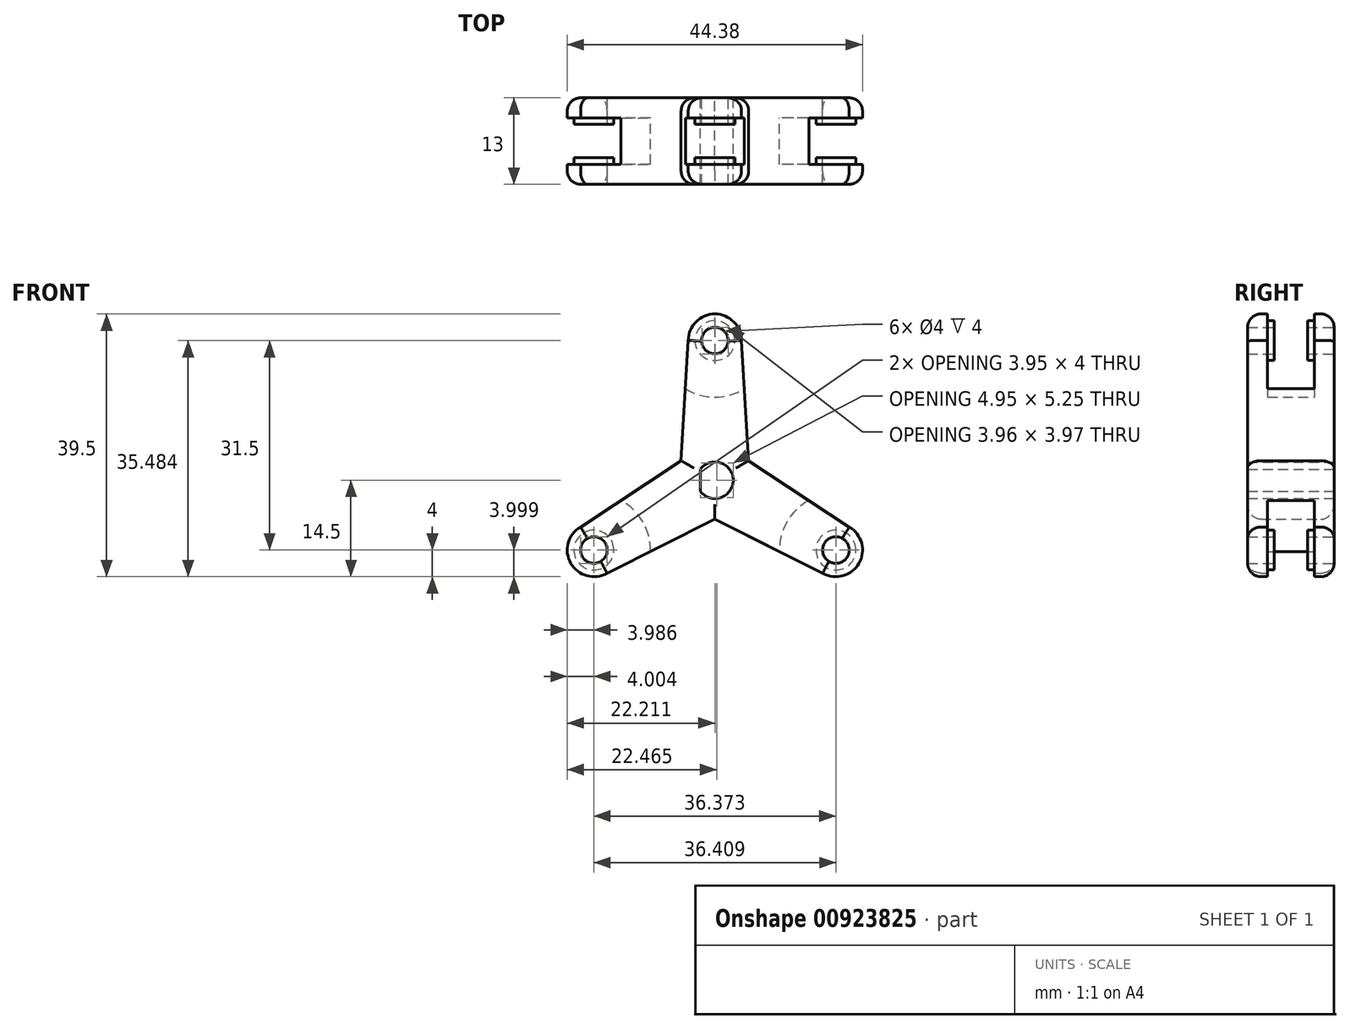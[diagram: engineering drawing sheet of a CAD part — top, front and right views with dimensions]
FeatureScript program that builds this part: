
annotation { "Feature Type Name" : "Feature", "Feature Type Description" : "" }
export const myFeature = defineFeature(function(context is Context, id is Id, definition is map)
    precondition{}
    {
        {
            var Q0;
            Q0=qCreatedBy(makeId("Front.planeOp"),FACE);
            var sketch = newSketch(context, id + "F0", { "sketchPlane" : qUnion([Q0])});
            skPoint(sketch, "E0", {"position": v(0, 27.5) * mm});
            skArc(sketch, "E1", {"start": v(-2.2, -1.65) * mm, "mid": v(2.75, 0) * mm, "end": v(-2.2, 1.65) * mm});
            skLineSegment(sketch, "E2", {"start": v(-2.2, 0) * mm, "end": v(-2.2, 1.65) * mm});
            skLineSegment(sketch, "E3", {"start": v(-2.2, 0) * mm, "end": v(-2.2, -1.65) * mm});
            skPoint(sketch, "E4", {"position": v(0, 21) * mm});
            skCircle(sketch, "E5", {"center": v(0, 21) * mm, "radius": 2 * mm});
            skCircle(sketch, "E6", {"center": v(0, 21) * mm, "radius": 3 * mm});
            skArc(sketch, "E7", {"start": v(-4.43, 13.75) * mm, "mid": v(0, 12.5) * mm, "end": v(4.43, 13.75) * mm});
            skPoint(sketch, "E8", {"position": v(0, 25) * mm});
            skArc(sketch, "E9", {"start": v(4, 21) * mm, "mid": v(0, 25) * mm, "end": v(-4, 21) * mm});
            skPoint(sketch, "E10", {"position": v(-4, 21) * mm});
            skPoint(sketch, "E11", {"position": v(4, 21) * mm});
            skLineSegment(sketch, "E12", {"start": v(-4, 21) * mm, "end": v(-5.26, 0) * mm});
            skLineSegment(sketch, "E13.MirrorCS", {"start": v(4, 21) * mm, "end": v(5.26, 0) * mm});
            skCircle(sketch, "E14.1.0", {"center": v(-18.19, -10.5) * mm, "radius": 2 * mm});
            skCircle(sketch, "E14.1.1", {"center": v(-18.19, -10.5) * mm, "radius": 3 * mm});
            skPoint(sketch, "E14.1.2", {"position": v(-20.19, -7.04) * mm});
            skPoint(sketch, "E14.1.3", {"position": v(-21.65, -12.5) * mm});
            skArc(sketch, "E14.1.4", {"start": v(-9.69, -10.71) * mm, "mid": v(-10.83, -6.25) * mm, "end": v(-14.12, -3.03) * mm});
            skArc(sketch, "E14.1.5", {"start": v(-20.19, -7.04) * mm, "mid": v(-21.65, -12.5) * mm, "end": v(-16.19, -13.96) * mm});
            skPoint(sketch, "E14.1.6", {"position": v(-16.19, -13.96) * mm});
            skLineSegment(sketch, "E14.1.7", {"start": v(-16.19, -13.96) * mm, "end": v(2.63, -4.55) * mm});
            skPoint(sketch, "E14.1.8", {"position": v(-18.19, -10.5) * mm});
            skLineSegment(sketch, "E14.1.9", {"start": v(-20.19, -7.04) * mm, "end": v(-2.63, 4.55) * mm});
            skCircle(sketch, "E14.2.0", {"center": v(18.19, -10.5) * mm, "radius": 2 * mm});
            skCircle(sketch, "E14.2.1", {"center": v(18.19, -10.5) * mm, "radius": 3 * mm});
            skPoint(sketch, "E14.2.2", {"position": v(16.19, -13.96) * mm});
            skPoint(sketch, "E14.2.3", {"position": v(21.65, -12.5) * mm});
            skArc(sketch, "E14.2.4", {"start": v(14.12, -3.03) * mm, "mid": v(10.83, -6.25) * mm, "end": v(9.69, -10.71) * mm});
            skArc(sketch, "E14.2.5", {"start": v(16.19, -13.96) * mm, "mid": v(21.65, -12.5) * mm, "end": v(20.19, -7.04) * mm});
            skPoint(sketch, "E14.2.6", {"position": v(20.19, -7.04) * mm});
            skLineSegment(sketch, "E14.2.7", {"start": v(20.19, -7.04) * mm, "end": v(2.63, 4.55) * mm});
            skPoint(sketch, "E14.2.8", {"position": v(18.19, -10.5) * mm});
            skLineSegment(sketch, "E14.2.9", {"start": v(16.19, -13.96) * mm, "end": v(-2.63, -4.55) * mm});
            skSolve(sketch);
        }
        {
            var Q0;
            Q0=makeQuery(id+"F0.imprint","IMPRINT",FACE,{"disambiguationData":[TD([[makeQuery(id+"F0.imprint","IMPRINT",EDGE,{"derivedFrom":sQuery(id+"F0.wireOp",EDGE,"E5")}),-1.0]])]});
            var Q1;
            Q1=makeQuery(id+"F0.imprint","IMPRINT",FACE,{"disambiguationData":[TD([[makeQuery(id+"F0.imprint","IMPRINT",EDGE,{"derivedFrom":sQuery(id+"F0.wireOp",EDGE,"E6")}),-1.0]])]});
            var Q2;
            Q2=makeQuery(id+"F0.imprint","IMPRINT",FACE,{"disambiguationData":[TD([[makeQuery(id+"F0.imprint","IMPRINT",EDGE,{"derivedFrom":sQuery(id+"F0.wireOp",EDGE,"E1")}),-1.0]])]});
            var Q3;
            Q3=makeQuery(id+"F0.imprint","IMPRINT",FACE,{"disambiguationData":[TD([[makeQuery(id+"F0.imprint","IMPRINT",EDGE,{"derivedFrom":sQuery(id+"F0.wireOp",EDGE,"E14.2.1")}),-1.0]])]});
            var Q4;
            Q4=makeQuery(id+"F0.imprint","IMPRINT",FACE,{"disambiguationData":[TD([[makeQuery(id+"F0.imprint","IMPRINT",EDGE,{"derivedFrom":sQuery(id+"F0.wireOp",EDGE,"E14.1.1")}),-1.0]])]});
            var Q5;
            Q5=makeQuery(id+"F0.imprint","IMPRINT",FACE,{"disambiguationData":[TD([[makeQuery(id+"F0.imprint","IMPRINT",EDGE,{"derivedFrom":sQuery(id+"F0.wireOp",EDGE,"E14.1.0")}),-1.0]])]});
            var Q6;
            Q6=makeQuery(id+"F0.imprint","IMPRINT",FACE,{"disambiguationData":[TD([[makeQuery(id+"F0.imprint","IMPRINT",EDGE,{"derivedFrom":sQuery(id+"F0.wireOp",EDGE,"E14.2.0")}),-1.0]])]});
            extrude(context, id + "F1", {"entities" : qUnion([Q0, Q1, Q2, Q3, Q4, Q5, Q6]), "depth" : 13 * mm, "offsetDistance" : 25 * mm});
        }
        {
            var Q0;
            Q0=makeQuery(id+"F0.imprint","IMPRINT",FACE,{"disambiguationData":[TD([[makeQuery(id+"F0.imprint","IMPRINT",EDGE,{"derivedFrom":sQuery(id+"F0.wireOp",EDGE,"E6")}),-1.0]])]});
            var Q1;
            Q1=makeQuery(id+"F0.imprint","IMPRINT",FACE,{"disambiguationData":[TD([[makeQuery(id+"F0.imprint","IMPRINT",EDGE,{"derivedFrom":sQuery(id+"F0.wireOp",EDGE,"E14.2.1")}),-1.0]])]});
            var Q2;
            Q2=makeQuery(id+"F0.imprint","IMPRINT",FACE,{"disambiguationData":[TD([[makeQuery(id+"F0.imprint","IMPRINT",EDGE,{"derivedFrom":sQuery(id+"F0.wireOp",EDGE,"E14.1.1")}),-1.0]])]});
            extrude(context, id + "F2", {"entities" : qUnion([Q0, Q1, Q2]), "operationType" : NewBodyOperationType.REMOVE, "endBound" : BoundingType.UP_TO_NEXT, "depth" : 3 * mm, "hasOffset" : true, "offsetDistance" : 3 * mm, "hasSecondDirection" : true, "secondDirectionOppositeDirection" : false, "secondDirectionDepth" : 3 * mm});
        }
        {
            var Q0;
            Q0=makeQuery(id+"F0.imprint","IMPRINT",FACE,{"disambiguationData":[TD([[makeQuery(id+"F0.imprint","IMPRINT",EDGE,{"derivedFrom":sQuery(id+"F0.wireOp",EDGE,"E14.2.0")}),-1.0]])]});
            var Q1;
            Q1=makeQuery(id+"F0.imprint","IMPRINT",FACE,{"disambiguationData":[TD([[makeQuery(id+"F0.imprint","IMPRINT",EDGE,{"derivedFrom":sQuery(id+"F0.wireOp",EDGE,"E5")}),-1.0]])]});
            var Q2;
            Q2=makeQuery(id+"F0.imprint","IMPRINT",FACE,{"disambiguationData":[TD([[makeQuery(id+"F0.imprint","IMPRINT",EDGE,{"derivedFrom":sQuery(id+"F0.wireOp",EDGE,"E14.1.0")}),-1.0]])]});
            extrude(context, id + "F3", {"entities" : qUnion([Q0, Q1, Q2]), "operationType" : NewBodyOperationType.REMOVE, "endBound" : BoundingType.UP_TO_NEXT, "depth" : 25 * mm, "hasOffset" : true, "offsetDistance" : 4 * mm, "hasSecondDirection" : true, "secondDirectionOppositeDirection" : false, "secondDirectionDepth" : 4 * mm});
        }
        {
            var Q0;
            Q0=makeQuery(id+"F1.opExtrude","CAP_EDGE",EDGE,{"disambiguationData":[OSD([sQuery(id+"F0.wireOp",EDGE,"E14.2.5")])],"isStart":false});
            var Q1;
            Q1=makeQuery(id+"F1.opExtrude","CAP_EDGE",EDGE,{"disambiguationData":[OSD([sQuery(id+"F0.wireOp",EDGE,"E14.1.5")])],"isStart":false});
            var Q2;
            Q2=makeQuery(id+"F1.opExtrude","CAP_EDGE",EDGE,{"disambiguationData":[OSD([sQuery(id+"F0.wireOp",EDGE,"E9")])],"isStart":false});
            var Q3;
            Q3=makeQuery(id+"F1.opExtrude","CAP_EDGE",EDGE,{"disambiguationData":[OSD([sQuery(id+"F0.wireOp",EDGE,"E14.2.5")])],"isStart":true});
            var Q4;
            Q4=makeQuery(id+"F1.opExtrude","CAP_EDGE",EDGE,{"disambiguationData":[OSD([sQuery(id+"F0.wireOp",EDGE,"E14.1.5")])],"isStart":true});
            var Q5;
            Q5=makeQuery(id+"F1.opExtrude","CAP_EDGE",EDGE,{"disambiguationData":[OSD([sQuery(id+"F0.wireOp",EDGE,"E9")])],"isStart":true});
            var Q6;
            Q6=makeQuery(id+"F2.boolean.opBoolean","COPY",EDGE,{"derivedFrom":makeQuery(id+"F2.opExtrude","SWEPT_EDGE",EDGE,{"disambiguationData":[OSD([sQuery(id+"F0.wireOp",EDGE,"E14.2.4"),sQuery(id+"F0.wireOp",EDGE,"E14.2.7")])]})});
            var Q7;
            Q7=makeQuery(id+"F2.boolean.opBoolean","COPY",EDGE,{"derivedFrom":makeQuery(id+"F2.opExtrude","SWEPT_EDGE",EDGE,{"disambiguationData":[OSD([sQuery(id+"F0.wireOp",EDGE,"E7"),sQuery(id+"F0.wireOp",EDGE,"E13.MirrorCS")])]})});
            var Q8;
            Q8=makeQuery(id+"F2.boolean.opBoolean","COPY",EDGE,{"derivedFrom":makeQuery(id+"F2.opExtrude","SWEPT_EDGE",EDGE,{"disambiguationData":[OSD([sQuery(id+"F0.wireOp",EDGE,"E14.2.4"),sQuery(id+"F0.wireOp",EDGE,"E14.2.9")])]})});
            var Q9;
            Q9=makeQuery(id+"F2.boolean.opBoolean","COPY",EDGE,{"derivedFrom":makeQuery(id+"F2.opExtrude","SWEPT_EDGE",EDGE,{"disambiguationData":[OSD([sQuery(id+"F0.wireOp",EDGE,"E14.1.4"),sQuery(id+"F0.wireOp",EDGE,"E14.1.7")])]})});
            var Q10;
            Q10=makeQuery(id+"F2.boolean.opBoolean","COPY",EDGE,{"derivedFrom":makeQuery(id+"F2.opExtrude","SWEPT_EDGE",EDGE,{"disambiguationData":[OSD([sQuery(id+"F0.wireOp",EDGE,"E14.1.4"),sQuery(id+"F0.wireOp",EDGE,"E14.1.9")])]})});
            var Q11;
            Q11=makeQuery(id+"F2.boolean.opBoolean","COPY",EDGE,{"derivedFrom":makeQuery(id+"F2.opExtrude","SWEPT_EDGE",EDGE,{"disambiguationData":[OSD([sQuery(id+"F0.wireOp",EDGE,"E7"),sQuery(id+"F0.wireOp",EDGE,"E12")])]})});
            fillet(context, id + "F4", {"entities" : qUnion([Q0, Q1, Q2, Q3, Q4, Q5, Q6, Q7, Q8, Q9, Q10, Q11]), "radius" : 2 * mm, "tangentPropagation" : true, "allowEdgeOverflow" : false});
        }
    });
